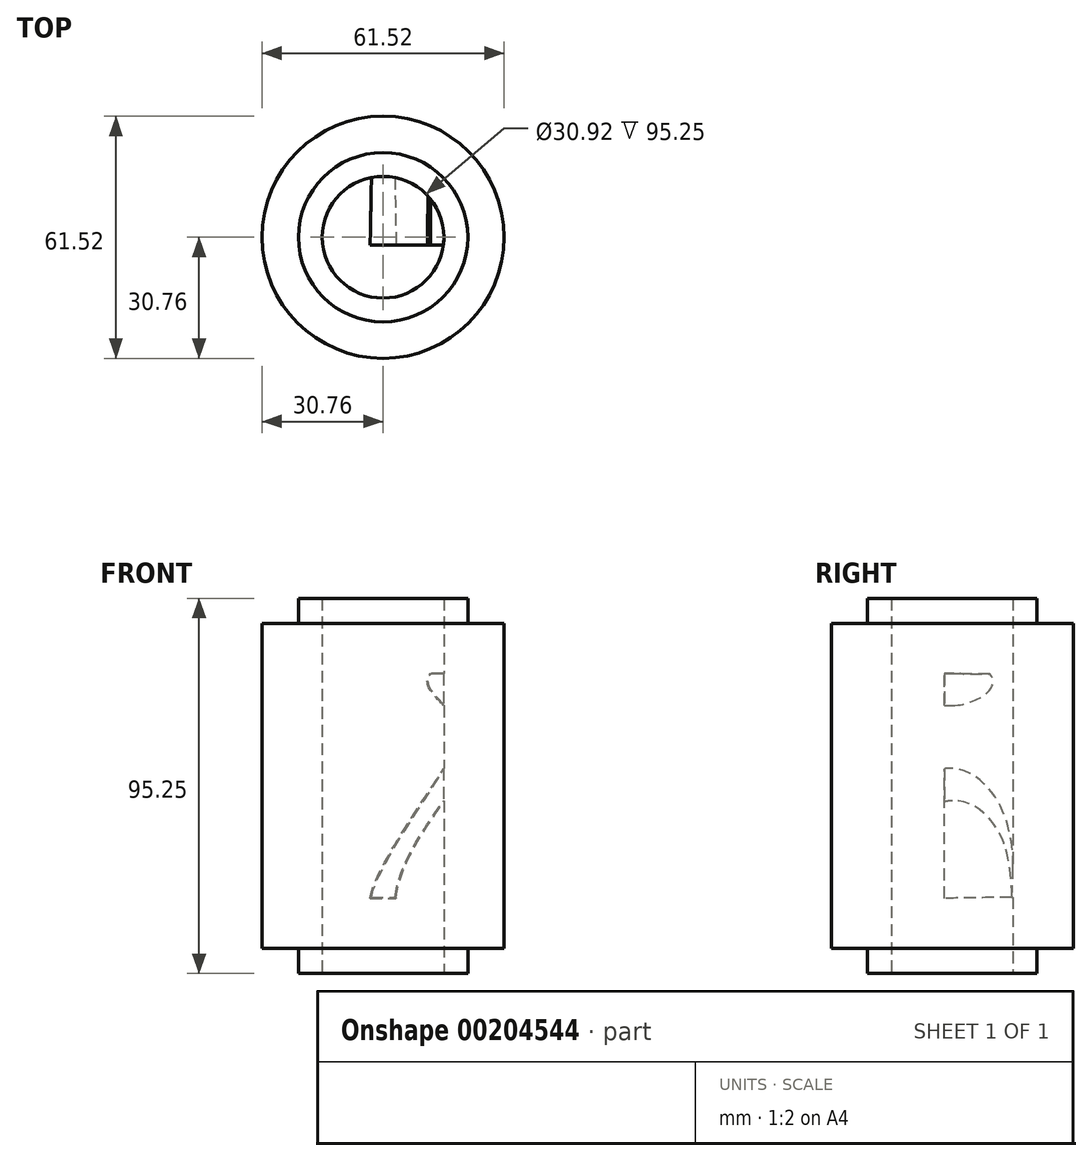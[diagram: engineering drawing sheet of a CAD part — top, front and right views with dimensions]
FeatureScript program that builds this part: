
annotation { "Feature Type Name" : "Feature", "Feature Type Description" : "" }
export const myFeature = defineFeature(function(context is Context, id is Id, definition is map)
    precondition{}
    {
        {
            assignVariable(context, id + "F0", {"name" : "Distance", "anyValue" : 2});
        }
        {
            var Q0;
            Q0=qCreatedBy(makeId("Top.planeOp"),FACE);
            var sketch = newSketch(context, id + "F1", { "sketchPlane" : qUnion([Q0])});
            skCircle(sketch, "E0", {"center": v(0, 0) * mm, "radius": 30.76 * mm});
            skCircle(sketch, "E1", {"center": v(0, 0) * mm, "radius": 15.46 * mm});
            skCircle(sketch, "E2", {"center": v(0, 0) * mm, "radius": 21.52 * mm});
            skSolve(sketch);
        }
        {
            var Q0;
            Q0 = qSketchRegion(id + "F1", true);
            extrude(context, id + "F2", {"entities" : qUnion([Q0]), "depth" : 82.55 * mm});
        }
        {
            var Q0;
            Q0=makeQuery(id+"F1.imprint","IMPRINT",FACE,{"disambiguationData":[TD([[makeQuery(id+"F1.imprint","IMPRINT",EDGE,{"derivedFrom":sQuery(id+"F1.wireOp",EDGE,"E1")}),-1.0]])]});
            extrude(context, id + "F3", {"entities" : qUnion([Q0]), "operationType" : NewBodyOperationType.ADD, "depth" : 88.9 * mm, "hasSecondDirection" : true, "secondDirectionOppositeDirection" : true, "secondDirectionDepth" : 6.35 * mm});
        }
        {
            var Q0;
            Q0=qCreatedBy(makeId("Front.planeOp"),FACE);
            cPlane(context, id + "F4", {"entities" : qUnion([Q0]), "cplaneType" : CPlaneType.OFFSET, "offset" : (getVariable(context, 'Distance')) * mm, "width" : 152.4 * mm, "height" : 152.4 * mm});
        }
        {
            var Q0;
            Q0=qCreatedBy(makeId("Front.planeOp"),FACE);
            var sketch = newSketch(context, id + "F5", { "sketchPlane" : qUnion([Q0])});
            skLineSegment(sketch, "E3", {"start": v(0, 0) * mm, "end": v(0, 85.06) * mm, "construction": true});
            skSolve(sketch);
        }
        {
            var Q0;
            Q0=qCreatedBy(id+"F4.planeOp",FACE);
            var sketch = newSketch(context, id + "F6", { "sketchPlane" : qUnion([Q0])});
            skLineSegment(sketch, "E4.0", {"start": v(-30.76, 82.55) * mm, "end": v(30.76, 82.55) * mm, "construction": true});
            skLineSegment(sketch, "E5.0", {"start": v(-30.76, 0) * mm, "end": v(30.76, 0) * mm, "construction": true});
            skLineSegment(sketch, "E6", {"start": v(-30.76, 69.85) * mm, "end": v(30.76, 69.85) * mm, "construction": true});
            skLineSegment(sketch, "E7", {"start": v(-30.76, 12.7) * mm, "end": v(30.76, 12.7) * mm, "construction": true});
            skLineSegment(sketch, "E8", {"start": v(-3.29, 12.7) * mm, "end": v(12.03, 69.85) * mm, "construction": true});
            skLineSegment(sketch, "E9", {"start": v(12.03, 69.85) * mm, "end": v(18.6, 69.85) * mm});
            skLineSegment(sketch, "E10", {"start": v(18.6, 69.85) * mm, "end": v(3.29, 12.7) * mm, "construction": true});
            skLineSegment(sketch, "E11", {"start": v(3.29, 12.7) * mm, "end": v(-3.29, 12.7) * mm});
            skFitSpline(sketch, "E12", {"points": [v(-3.29, 12.7) * mm, v(9.83, 37.1) * mm, v(17.84, 58.45) * mm, v(12.03, 69.85) * mm], "startDerivative": vector(2.42, 33.48) * mm, "endDerivative": vector(35.62, 43.03) * mm});
            skLineSegment(sketch, "E13", {"start": v(0, 12.7) * mm, "end": v(15.31, 69.85) * mm, "construction": true});
            skFitSpline(sketch, "E14", {"points": [v(3.29, 12.7) * mm, v(15.25, 37.1) * mm, v(23.29, 58.45) * mm, v(18.6, 69.85) * mm], "startDerivative": vector(7.96, 67.13) * mm, "endDerivative": vector(25.32, 54.3) * mm});
            skSolve(sketch);
        }
        {
            var Q0;
            Q0=makeQuery(id+"F6.imprint","IMPRINT",FACE,{"disambiguationData":[TD([[makeQuery(id+"F6.imprint","IMPRINT",EDGE,{"derivedFrom":sQuery(id+"F6.wireOp",EDGE,"E9")}),-1.0]])]});
            var Q1;
            Q1=makeQuery(id+"F2.opExtrude","SWEPT_BODY",BODY,{"disambiguationData":[OSD([sQuery(id+"F1.wireOp",EDGE,"E0")])]});
            extrude(context, id + "F7", {"entities" : qUnion([Q0]), "operationType" : NewBodyOperationType.ADD, "endBound" : BoundingType.UP_TO_BODY, "oppositeDirection" : true, "endBoundEntityBody" : qUnion([Q1]), "depth" : 25.4 * mm, "hasDraft" : true, "draftAngle" : 1 * degree, "draftPullDirection" : true});
        }
    });
